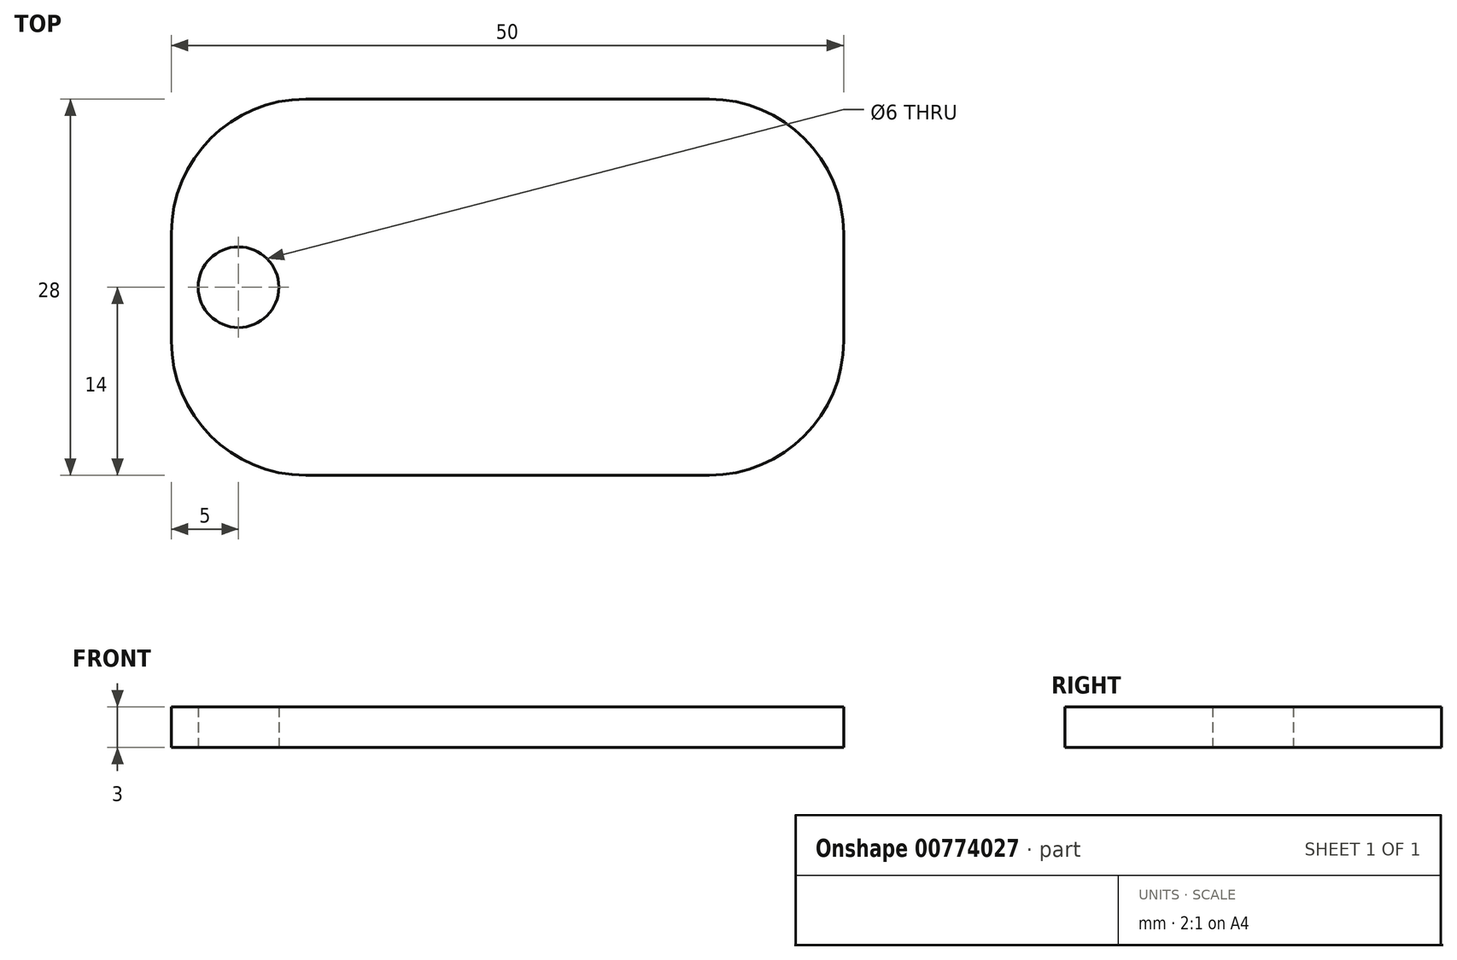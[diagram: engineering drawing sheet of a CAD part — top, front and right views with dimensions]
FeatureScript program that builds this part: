
annotation { "Feature Type Name" : "Feature", "Feature Type Description" : "" }
export const myFeature = defineFeature(function(context is Context, id is Id, definition is map)
    precondition{}
    {
        {
            var Q0;
            Q0=qCreatedBy(makeId("Top.planeOp"),FACE);
            var sketch = newSketch(context, id + "F0", { "sketchPlane" : qUnion([Q0])});
            skLineSegment(sketch, "E0.bottom", {"start": v(-15, 14) * mm, "end": v(15, 14) * mm});
            skLineSegment(sketch, "E0.top", {"start": v(-15, -14) * mm, "end": v(15, -14) * mm});
            skLineSegment(sketch, "E0.left", {"start": v(-25, 4) * mm, "end": v(-25, -4) * mm});
            skLineSegment(sketch, "E0.right", {"start": v(25, 4) * mm, "end": v(25, -4) * mm});
            skPoint(sketch, "E1.visualSharp", {"position": v(-25, 14) * mm});
            skArc(sketch, "E1.filletArc", {"start": v(-15, 14) * mm, "mid": v(-22.07, 11.07) * mm, "end": v(-25, 4) * mm});
            skPoint(sketch, "E2.visualSharp", {"position": v(-25, -14) * mm});
            skArc(sketch, "E2.filletArc", {"start": v(-25, -4) * mm, "mid": v(-22.07, -11.07) * mm, "end": v(-15, -14) * mm});
            skPoint(sketch, "E3.visualSharp", {"position": v(25, -14) * mm});
            skArc(sketch, "E3.filletArc", {"start": v(15, -14) * mm, "mid": v(22.07, -11.07) * mm, "end": v(25, -4) * mm});
            skPoint(sketch, "E4.visualSharp", {"position": v(25, 14) * mm});
            skArc(sketch, "E4.filletArc", {"start": v(25, 4) * mm, "mid": v(22.07, 11.07) * mm, "end": v(15, 14) * mm});
            skCircle(sketch, "E5", {"center": v(-20, 0) * mm, "radius": 3 * mm});
            skSolve(sketch);
        }
        {
            var Q0;
            Q0=makeQuery(id+"F0.imprint","IMPRINT",FACE,{"disambiguationData":[TD([[makeQuery(id+"F0.imprint","IMPRINT",EDGE,{"derivedFrom":sQuery(id+"F0.wireOp",EDGE,"E0.bottom")}),-1.0]])]});
            extrude(context, id + "F1", {"entities" : qUnion([Q0]), "depth" : 3 * mm, "offsetDistance" : 25 * mm});
        }
    });
